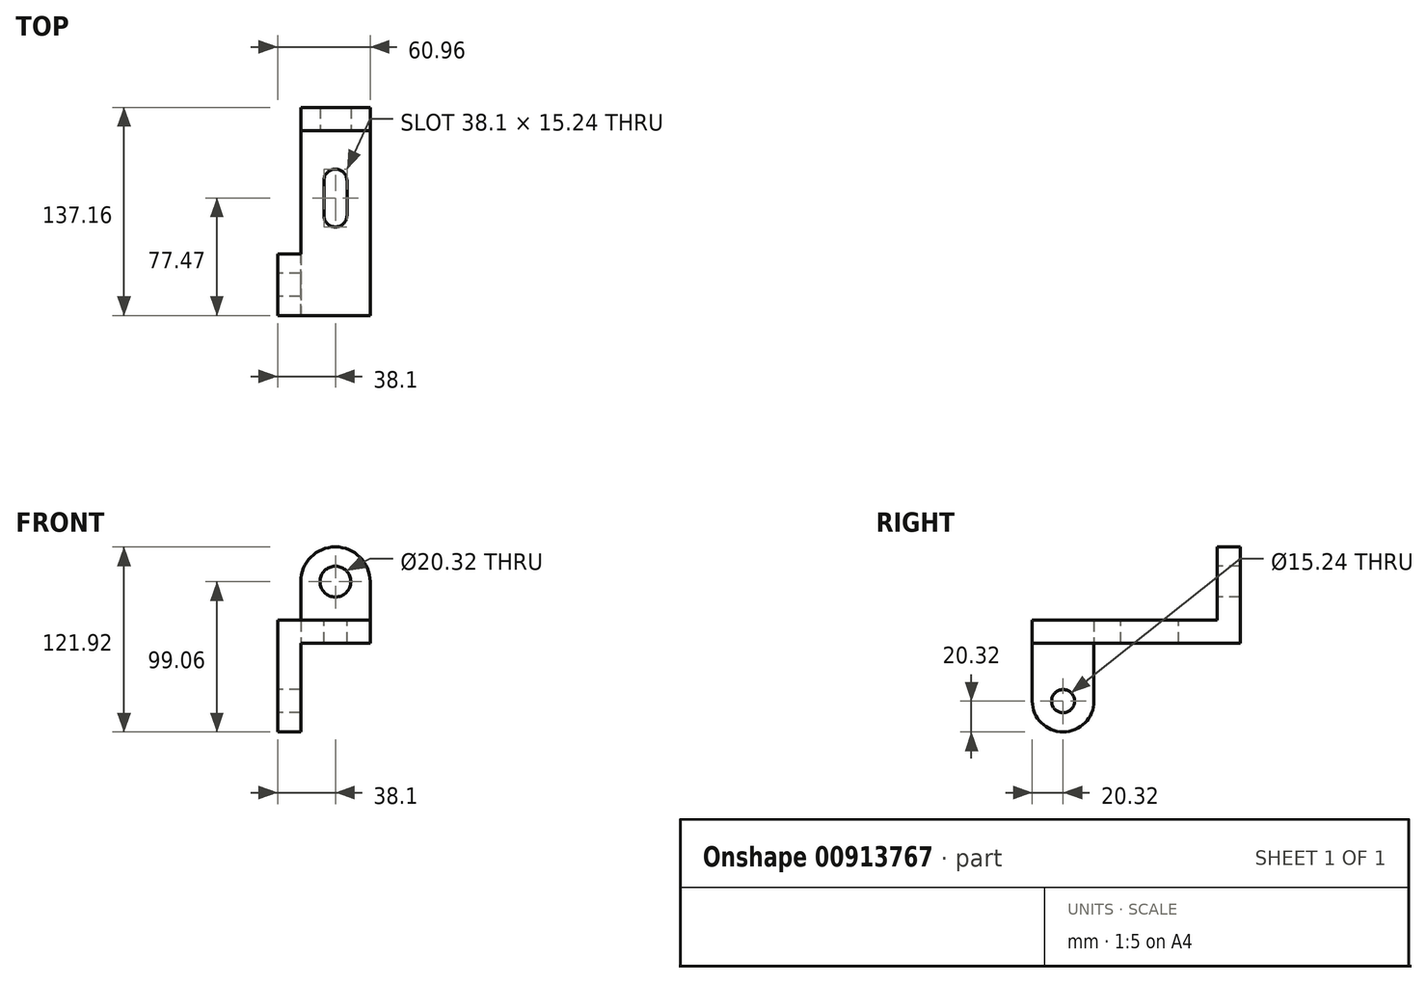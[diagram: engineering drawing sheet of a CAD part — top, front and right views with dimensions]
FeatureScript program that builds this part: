
annotation { "Feature Type Name" : "Feature", "Feature Type Description" : "" }
export const myFeature = defineFeature(function(context is Context, id is Id, definition is map)
    precondition{}
    {
        {
            var Q0;
            Q0=qCreatedBy(makeId("Top.planeOp"),FACE);
            var sketch = newSketch(context, id + "F0", { "sketchPlane" : qUnion([Q0])});
            skLineSegment(sketch, "E0", {"start": v(-30.48, 68.58) * mm, "end": v(-30.48, -27.94) * mm});
            skLineSegment(sketch, "E1", {"start": v(-30.48, 68.58) * mm, "end": v(15.24, 68.58) * mm});
            skLineSegment(sketch, "E2", {"start": v(-45.72, -68.58) * mm, "end": v(-45.72, -27.94) * mm});
            skLineSegment(sketch, "E3", {"start": v(-45.72, -27.94) * mm, "end": v(-30.48, -27.94) * mm});
            skLineSegment(sketch, "E4", {"start": v(15.24, -68.58) * mm, "end": v(-45.72, -68.58) * mm});
            skLineSegment(sketch, "E5", {"start": v(15.24, 68.58) * mm, "end": v(15.24, -68.58) * mm});
            skSolve(sketch);
        }
        {
            var Q0;
            Q0 = qSketchRegion(id + "F0", true);
            extrude(context, id + "F1", {"entities" : qUnion([Q0]), "depth" : 15.24 * mm, "offsetDistance" : 25.4 * mm});
        }
        {
            var Q0;
            Q0=makeQuery(id+"F1.opExtrude","CAP_FACE",FACE,{"disambiguationData":[OSD([sQuery(id+"F0.wireOp",EDGE,"E0"),sQuery(id+"F0.wireOp",EDGE,"E1"),sQuery(id+"F0.wireOp",EDGE,"VoiDpAs3-1DRk-zy0O-66wL-6Vqmmt0H40B9"),sQuery(id+"F0.wireOp",EDGE,"yMA1i0tk-afwQ-v4ox-1sYv-qTezlCexKwUL"),sQuery(id+"F0.wireOp",EDGE,"k7M3sByT-VUhO-220q-02cH-4DluD7k4yhj6"),sQuery(id+"F0.wireOp",EDGE,"E2"),sQuery(id+"F0.wireOp",EDGE,"E3")])],"isStart":false});
            var sketch = newSketch(context, id + "F2", { "sketchPlane" : qUnion([Q0])});
            skLineSegment(sketch, "E6", {"start": v(-30.48, 68.58) * mm, "end": v(-30.48, 68.58) * mm});
            skLineSegment(sketch, "E7", {"start": v(-30.48, 53.34) * mm, "end": v(-30.48, 53.34) * mm});
            skLineSegment(sketch, "E8.bottom", {"start": v(-30.48, 53.34) * mm, "end": v(15.24, 53.34) * mm});
            skLineSegment(sketch, "E8.top", {"start": v(-30.48, 68.58) * mm, "end": v(15.24, 68.58) * mm});
            skLineSegment(sketch, "E8.left", {"start": v(-30.48, 53.34) * mm, "end": v(-30.48, 68.58) * mm});
            skLineSegment(sketch, "E8.right", {"start": v(15.24, 53.34) * mm, "end": v(15.24, 68.58) * mm});
            skSolve(sketch);
        }
        {
            var Q0;
            Q0 = qSketchRegion(id + "F2", true);
            extrude(context, id + "F3", {"entities" : qUnion([Q0]), "operationType" : NewBodyOperationType.ADD, "depth" : 48.26 * mm, "offsetDistance" : 25.4 * mm});
        }
        {
            var Q0;
            Q0=makeQuery(id+"F3.opExtrude","SWEPT_FACE",FACE,{"disambiguationData":[OSD([sQuery(id+"F2.wireOp",EDGE,"E8.bottom")])]});
            var sketch = newSketch(context, id + "F4", { "sketchPlane" : qUnion([Q0])});
            skArc(sketch, "E9", {"start": v(15.24, 40.64) * mm, "mid": v(-7.62, 63.5) * mm, "end": v(-30.48, 40.64) * mm});
            skCircle(sketch, "E10", {"center": v(-7.62, 40.64) * mm, "radius": 10.16 * mm});
            skSolve(sketch);
        }
        {
            var Q0;
            {var subQ0=sQuery(id+"F4.wireOp",EDGE,"E9");var subQ1=sQuery(id+"F2.wireOp",EDGE,"E8.bottom");var subQ4=makeQuery(id+"F3.opExtrude","CAP_EDGE",EDGE,{"disambiguationData":[OSD([subQ1])],"isStart":false});var subQ5=makeQuery(id+"F4.imprint","INTERSECT",VERTEX,{"derivedFrom":[subQ4,subQ0]});Q0=makeQuery(id+"F4.imprint","IMPRINT",FACE,{"disambiguationData":[TD([[makeQuery(id+"F4.imprint","IMPRINT",EDGE,{"disambiguationData":[TD([[subQ5,1.0]])],"derivedFrom":subQ0}),-1.0]])]});}
            var Q1;
            {var subQ0=sQuery(id+"F4.wireOp",EDGE,"E9");var subQ1=sQuery(id+"F2.wireOp",EDGE,"E8.bottom");var subQ4=makeQuery(id+"F3.opExtrude","CAP_EDGE",EDGE,{"disambiguationData":[OSD([subQ1])],"isStart":false});var subQ5=makeQuery(id+"F4.imprint","INTERSECT",VERTEX,{"derivedFrom":[subQ4,subQ0]});Q1=makeQuery(id+"F4.imprint","IMPRINT",FACE,{"disambiguationData":[TD([[makeQuery(id+"F4.imprint","IMPRINT",EDGE,{"disambiguationData":[TD([[subQ5,-1.0]])],"derivedFrom":subQ0}),-1.0]])]});}
            var Q2;
            Q2=makeQuery(id+"F4.imprint","IMPRINT",FACE,{"disambiguationData":[TD([[makeQuery(id+"F4.imprint","IMPRINT",EDGE,{"derivedFrom":sQuery(id+"F4.wireOp",EDGE,"E10")}),1.0]])]});
            extrude(context, id + "F5", {"entities" : qUnion([Q0, Q1, Q2]), "operationType" : NewBodyOperationType.REMOVE, "endBound" : BoundingType.UP_TO_NEXT, "oppositeDirection" : true, "depth" : 25.4 * mm, "offsetDistance" : 25.4 * mm});
        }
        {
            var Q0;
            Q0=makeQuery(id+"F1.opExtrude","SWEPT_FACE",FACE,{"disambiguationData":[OSD([sQuery(id+"F0.wireOp",EDGE,"E2")])]});
            var sketch = newSketch(context, id + "F6", { "sketchPlane" : qUnion([Q0])});
            skLineSegment(sketch, "E11", {"start": v(68.58, 0) * mm, "end": v(68.58, -58.42) * mm});
            skLineSegment(sketch, "E12", {"start": v(27.94, 0) * mm, "end": v(27.94, -58.42) * mm});
            skLineSegment(sketch, "E13", {"start": v(27.94, -58.42) * mm, "end": v(68.58, -58.42) * mm});
            skSolve(sketch);
        }
        {
            var Q0;
            Q0=makeQuery(id+"F6.imprint","IMPRINT",FACE,{"disambiguationData":[TD([[makeQuery(id+"F6.imprint","IMPRINT",EDGE,{"derivedFrom":sQuery(id+"F6.wireOp",EDGE,"E11")}),-1.0]])]});
            extrude(context, id + "F7", {"entities" : qUnion([Q0]), "operationType" : NewBodyOperationType.ADD, "oppositeDirection" : true, "depth" : 15.24 * mm, "offsetDistance" : 25.4 * mm});
        }
        {
            var Q0;
            {var subQ0=sQuery(id+"F0.wireOp",EDGE,"E2");Q0=makeQuery(id+"F7.boolean.opBoolean","MERGE",FACE,{"derivedFrom":[makeQuery(id+"F1.opExtrude","SWEPT_FACE",FACE,{"disambiguationData":[OSD([subQ0])]}),makeQuery(id+"F7.opExtrude","CAP_FACE",FACE,{"disambiguationData":[OSD([subQ0,sQuery(id+"F6.wireOp",EDGE,"E11"),sQuery(id+"F6.wireOp",EDGE,"E12"),sQuery(id+"F6.wireOp",EDGE,"E13")])],"isStart":true})]});}
            var sketch = newSketch(context, id + "F8", { "sketchPlane" : qUnion([Q0])});
            skArc(sketch, "E14", {"start": v(27.94, -38.1) * mm, "mid": v(48.26, -58.42) * mm, "end": v(68.58, -38.1) * mm});
            skCircle(sketch, "E15", {"center": v(48.26, -38.1) * mm, "radius": 7.62 * mm});
            skSolve(sketch);
        }
        {
            var Q0;
            {var subQ0=sQuery(id+"F8.wireOp",EDGE,"E14");var subQ3=makeQuery(id+"F7.opExtrude","CAP_EDGE",EDGE,{"disambiguationData":[OSD([sQuery(id+"F6.wireOp",EDGE,"E13")])],"isStart":true});var subQ4=makeQuery(id+"F8.imprint","INTERSECT",VERTEX,{"derivedFrom":[subQ3,subQ0]});Q0=makeQuery(id+"F8.imprint","IMPRINT",FACE,{"disambiguationData":[TD([[makeQuery(id+"F8.imprint","IMPRINT",EDGE,{"disambiguationData":[TD([[subQ4,-1.0]])],"derivedFrom":subQ0}),-1.0]])]});}
            var Q1;
            {var subQ0=sQuery(id+"F8.wireOp",EDGE,"E14");var subQ3=makeQuery(id+"F7.opExtrude","CAP_EDGE",EDGE,{"disambiguationData":[OSD([sQuery(id+"F6.wireOp",EDGE,"E13")])],"isStart":true});var subQ4=makeQuery(id+"F8.imprint","INTERSECT",VERTEX,{"derivedFrom":[subQ3,subQ0]});Q1=makeQuery(id+"F8.imprint","IMPRINT",FACE,{"disambiguationData":[TD([[makeQuery(id+"F8.imprint","IMPRINT",EDGE,{"disambiguationData":[TD([[subQ4,1.0]])],"derivedFrom":subQ0}),-1.0]])]});}
            var Q2;
            Q2=makeQuery(id+"F8.imprint","IMPRINT",FACE,{"disambiguationData":[TD([[makeQuery(id+"F8.imprint","IMPRINT",EDGE,{"derivedFrom":sQuery(id+"F8.wireOp",EDGE,"E15")}),1.0]])]});
            extrude(context, id + "F9", {"entities" : qUnion([Q0, Q1, Q2]), "operationType" : NewBodyOperationType.REMOVE, "endBound" : BoundingType.UP_TO_NEXT, "oppositeDirection" : true, "depth" : 25.4 * mm, "offsetDistance" : 25.4 * mm});
        }
        {
            var Q0;
            Q0=makeQuery(id+"F1.opExtrude","CAP_FACE",FACE,{"disambiguationData":[OSD([sQuery(id+"F0.wireOp",EDGE,"E0"),sQuery(id+"F0.wireOp",EDGE,"E1"),sQuery(id+"F0.wireOp",EDGE,"E2"),sQuery(id+"F0.wireOp",EDGE,"E3"),sQuery(id+"F0.wireOp",EDGE,"E4"),sQuery(id+"F0.wireOp",EDGE,"E5")])],"isStart":false});
            var sketch = newSketch(context, id + "F10", { "sketchPlane" : qUnion([Q0])});
            skLineSegment(sketch, "E16", {"start": v(-7.62, 53.34) * mm, "end": v(-7.62, 20.32) * mm});
            skLineSegment(sketch, "E17", {"start": v(-15.24, 20.32) * mm, "end": v(-15.24, -2.54) * mm});
            skLineSegment(sketch, "E18", {"start": v(0, -2.54) * mm, "end": v(0, 20.32) * mm});
            skArc(sketch, "E19", {"start": v(0, 20.32) * mm, "mid": v(-7.62, 27.94) * mm, "end": v(-15.24, 20.32) * mm});
            skArc(sketch, "E20", {"start": v(-15.24, -2.54) * mm, "mid": v(-7.62, -10.16) * mm, "end": v(0, -2.54) * mm});
            skSolve(sketch);
        }
        {
            var Q0;
            {var subQ1=sQuery(id+"F10.wireOp",EDGE,"E17");Q0=makeQuery(id+"F10.imprint","IMPRINT",FACE,{"disambiguationData":[TD([[makeQuery(id+"F10.imprint","IMPRINT",EDGE,{"derivedFrom":subQ1}),1.0]])]});}
            extrude(context, id + "F11", {"entities" : qUnion([Q0]), "operationType" : NewBodyOperationType.REMOVE, "endBound" : BoundingType.UP_TO_NEXT, "oppositeDirection" : true, "depth" : 25.4 * mm, "offsetDistance" : 25.4 * mm});
        }
    });
